# Revit family: P500147-015-30
name_source: partatom
category: Lighting Fixtures
revit_build: Autodesk Revit 2014 (Build: 20130308_1515(x64)
units: mm (PartAtom-declared; Revit-internal decimal feet)

## types (1)
- P500148-015-30
    Apparent Load = 17 VA
    Assembly Code = D5020200
    Color Filter = 16777215
    Connector Description = Lighting Connector
    Default Elevation = 48"
    Description = A distinctive classic globe pendant is accented by a striking metal polished chrome cap. The cap holds
a beautiful opal glass shade ready to emit gentle illumination. This versatile pendant can be displayed
as a single fixture or in groups of two or more to create a custom lighting design for your home.
    Diameter = 11 5/8"
    Dimming Lamp Color Temperature Shift = <None>
    Fixture distribution = Direct
    Glass = Hubbell - Glass
    Height = 13 1/2"
    Housing Material = Paint - Hubbell - Light Silver
    Lamp = A-19
    Load Classification = Lighting
    Manufacturer = Progress Lighting
    Model = P500148-015-30
    Photometric Web File = generic
    Power Factor = 1
    Product Documentation Link = https://hubbellcdn.com
    Product Link = https://www.hubbell.com
    Specifications = Polished Chrome (-015) (Plated)
• Steel Construction
• Opal Glass Globe
• The cap holds a beautiful opal glass shade ready to emit gentle illumination.
• A distinctive classic globe pendant is accented by a striking metal polished chrome cap.
• This versatile pendant can be displayed as a single fixture or in groups of two or more to create a
custom lighting design for your home.
• Ideal for any foyer, kitchen, or dining room.
• Perfect for mid-century modern, transitional, modern, or contemporary settings.
• Measures 11-5/8-inch width by 13-1/2-inch height.
• Overall length with cord is 136-1/2”
• Uses one LED bulb that is included (17w max).
• Able to be fully dimmable with dimmable bulbs.
• Includes installation instructions and mounting hardware.
• Progress Lighting products are designed for exceptional quality, reliability, and functionality.
• Canopy covers a standard 4 inch octagonal recessed outlet box
• Mounting 1/8 IP Mounting Plate for outlet box included
• 10 feet of wire supplied
• ENERGY STAR® qualified
• Meets California Title 24 JA8-2016
    String = Paint - Hubbell - White Texture
    Tilt Angle = 60.00°
    URL = https://www.hubbell.com
    Voltage = 120 V
    Warranty = 5 years Warranty
    Wattage Comments = 17
    Watts = 17 W

## geometry (parser evidence)
native form markers: Sweep x6
no freeform markers — native parametric forms only
